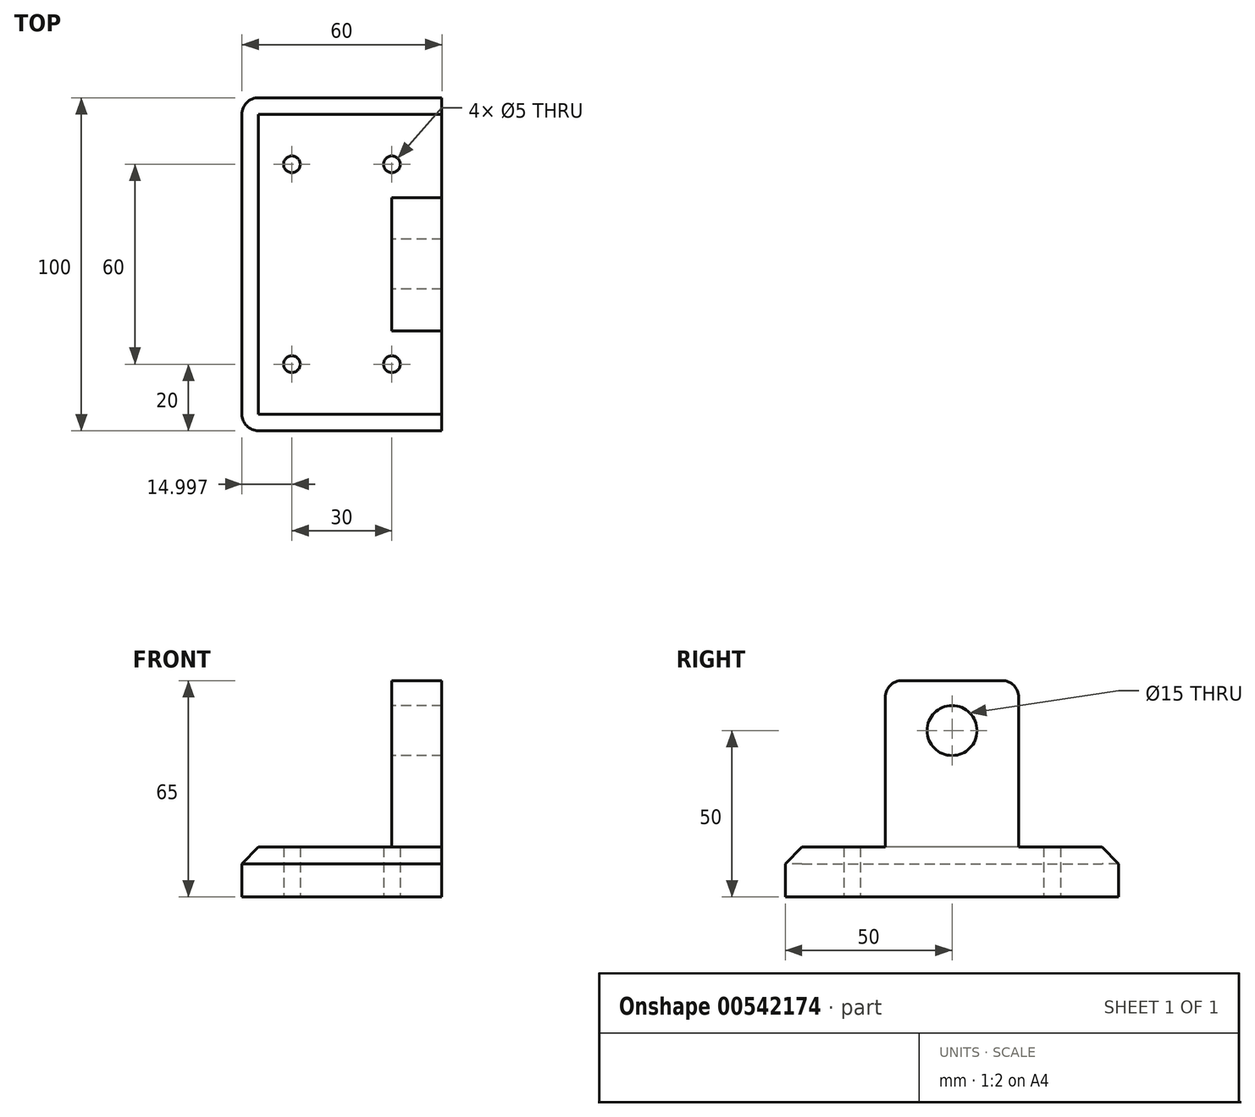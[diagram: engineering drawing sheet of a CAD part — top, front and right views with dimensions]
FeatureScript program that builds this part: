
annotation { "Feature Type Name" : "Feature", "Feature Type Description" : "" }
export const myFeature = defineFeature(function(context is Context, id is Id, definition is map)
    precondition{}
    {
        {
            var Q0;
            Q0=qCreatedBy(makeId("Top.planeOp"),FACE);
            var sketch = newSketch(context, id + "F0", { "sketchPlane" : qUnion([Q0])});
            skLineSegment(sketch, "E0.bottom", {"start": v(-60.08, 51.59) * mm, "end": v(-5.08, 51.59) * mm});
            skLineSegment(sketch, "E0.top", {"start": v(-60.08, -48.41) * mm, "end": v(-5.08, -48.41) * mm});
            skLineSegment(sketch, "E0.left", {"start": v(-65.08, 46.59) * mm, "end": v(-65.08, -43.41) * mm});
            skLineSegment(sketch, "E0.right", {"start": v(-5.08, 51.59) * mm, "end": v(-5.08, -48.41) * mm});
            skPoint(sketch, "E1.visualSharp", {"position": v(-65.08, 51.59) * mm});
            skArc(sketch, "E1.filletArc", {"start": v(-60.08, 51.59) * mm, "mid": v(-63.62, 50.13) * mm, "end": v(-65.08, 46.59) * mm});
            skPoint(sketch, "E2.visualSharp", {"position": v(-65.08, -48.41) * mm});
            skArc(sketch, "E2.filletArc", {"start": v(-65.08, -43.41) * mm, "mid": v(-63.62, -46.95) * mm, "end": v(-60.08, -48.41) * mm});
            skSolve(sketch);
        }
        {
            var Q0;
            Q0 = qSketchRegion(id + "F0", true);
            extrude(context, id + "F1", {"entities" : qUnion([Q0]), "depth" : 15 * mm, "offsetDistance" : 25 * mm});
        }
        {
            var Q0;
            Q0=makeQuery(id+"F1.opExtrude","SWEPT_FACE",FACE,{"disambiguationData":[OSD([sQuery(id+"F0.wireOp",EDGE,"E0.right")])]});
            var sketch = newSketch(context, id + "F2", { "sketchPlane" : qUnion([Q0])});
            skLineSegment(sketch, "E3.bottom", {"start": v(-18.41, 15) * mm, "end": v(21.59, 15) * mm});
            skLineSegment(sketch, "E3.top", {"start": v(-18.41, 65) * mm, "end": v(21.59, 65) * mm});
            skLineSegment(sketch, "E3.left", {"start": v(-18.41, 15) * mm, "end": v(-18.41, 65) * mm});
            skLineSegment(sketch, "E3.right", {"start": v(21.59, 15) * mm, "end": v(21.59, 65) * mm});
            skSolve(sketch);
        }
        {
            var Q0;
            Q0=makeQuery(id+"F2.imprint","IMPRINT",FACE,{"disambiguationData":[TD([[makeQuery(id+"F2.imprint","IMPRINT",EDGE,{"derivedFrom":sQuery(id+"F2.wireOp",EDGE,"E3.bottom")}),-1.0]])]});
            extrude(context, id + "F3", {"entities" : qUnion([Q0]), "operationType" : NewBodyOperationType.ADD, "oppositeDirection" : true, "depth" : 15 * mm, "offsetDistance" : 25 * mm});
        }
        {
            var Q0;
            Q0=makeQuery(id+"F3.opExtrude","SWEPT_EDGE",EDGE,{"disambiguationData":[OSD([sQuery(id+"F2.wireOp",EDGE,"E3.top"),sQuery(id+"F2.wireOp",EDGE,"E3.right")])]});
            var Q1;
            Q1=makeQuery(id+"F3.opExtrude","SWEPT_EDGE",EDGE,{"disambiguationData":[OSD([sQuery(id+"F2.wireOp",EDGE,"E3.top"),sQuery(id+"F2.wireOp",EDGE,"E3.left")])]});
            var Q2;
            Q2=makeQuery(id+"F3.opExtrude","SWEPT_EDGE",EDGE,{"disambiguationData":[OSD([sQuery(id+"F0.wireOp",EDGE,"E0.right"),sQuery(id+"F2.wireOp",EDGE,"E3.bottom"),sQuery(id+"F2.wireOp",EDGE,"E3.left")])]});
            var Q3;
            Q3=makeQuery(id+"F3.opExtrude","CAP_EDGE",EDGE,{"disambiguationData":[OSD([sQuery(id+"F2.wireOp",EDGE,"E3.bottom")])],"isStart":false});
            var Q4;
            Q4=makeQuery(id+"F3.opExtrude","SWEPT_EDGE",EDGE,{"disambiguationData":[OSD([sQuery(id+"F0.wireOp",EDGE,"E0.right"),sQuery(id+"F2.wireOp",EDGE,"E3.bottom"),sQuery(id+"F2.wireOp",EDGE,"E3.right")])]});
            fillet(context, id + "F4", {"entities" : qUnion([Q0, Q1, Q2, Q3, Q4]), "radius" : 5 * mm, "tangentPropagation" : true, "allowEdgeOverflow" : false});
        }
        {
            var Q0;
            Q0=makeQuery(id+"F1.opExtrude","CAP_EDGE",EDGE,{"disambiguationData":[OSD([sQuery(id+"F0.wireOp",EDGE,"E0.bottom")])],"isStart":false});
            chamfer(context, id + "F5", {"entities" : qUnion([Q0]), "width" : 5 * mm, "tangentPropagation" : true});
        }
        {
            var Q0;
            Q0=makeQuery(id+"F3.opExtrude","CAP_FACE",FACE,{"disambiguationData":[OSD([sQuery(id+"F2.wireOp",EDGE,"E3.bottom"),sQuery(id+"F2.wireOp",EDGE,"E3.top"),sQuery(id+"F2.wireOp",EDGE,"E3.left"),sQuery(id+"F2.wireOp",EDGE,"E3.right")])],"isStart":false});
            var sketch = newSketch(context, id + "F6", { "sketchPlane" : qUnion([Q0])});
            skLineSegment(sketch, "E4", {"start": v(-1.59, 65) * mm, "end": v(-1.59, 20) * mm, "construction": true});
            skCircle(sketch, "E5", {"center": v(-1.59, 50) * mm, "radius": 7.5 * mm});
            skSolve(sketch);
        }
        {
            var Q0;
            Q0=makeQuery(id+"F6.imprint","IMPRINT",FACE,{"disambiguationData":[TD([[makeQuery(id+"F6.imprint","IMPRINT",EDGE,{"derivedFrom":sQuery(id+"F6.wireOp",EDGE,"E5")}),1.0]])]});
            extrude(context, id + "F7", {"entities" : qUnion([Q0]), "operationType" : NewBodyOperationType.REMOVE, "oppositeDirection" : true, "depth" : 25 * mm, "offsetDistance" : 25 * mm});
        }
        {
            var Q0;
            Q0=makeQuery(id+"F1.opExtrude","CAP_FACE",FACE,{"disambiguationData":[OSD([sQuery(id+"F0.wireOp",EDGE,"E0.bottom"),sQuery(id+"F0.wireOp",EDGE,"E0.top"),sQuery(id+"F0.wireOp",EDGE,"E0.left"),sQuery(id+"F0.wireOp",EDGE,"E0.right"),sQuery(id+"F0.wireOp",EDGE,"E1.filletArc"),sQuery(id+"F0.wireOp",EDGE,"E2.filletArc")])],"isStart":true});
            var sketch = newSketch(context, id + "F8", { "sketchPlane" : qUnion([Q0])});
            skCircle(sketch, "E6", {"center": v(-50.08, 28.41) * mm, "radius": 2.5 * mm});
            skCircle(sketch, "E7.0.1.0", {"center": v(-50.08, -31.59) * mm, "radius": 2.5 * mm});
            skCircle(sketch, "E7.1.0.0", {"center": v(-20.08, 28.41) * mm, "radius": 2.5 * mm});
            skCircle(sketch, "E7.1.1.0", {"center": v(-20.08, -31.59) * mm, "radius": 2.5 * mm});
            skLineSegment(sketch, "E7.direction1", {"start": v(-50.08, 28.41) * mm, "end": v(-20.08, 28.41) * mm, "construction": true});
            skLineSegment(sketch, "E7.direction2", {"start": v(-50.08, 28.41) * mm, "end": v(-50.08, -31.59) * mm, "construction": true});
            skSolve(sketch);
        }
        {
            var Q0;
            Q0=makeQuery(id+"F8.imprint","IMPRINT",FACE,{"disambiguationData":[TD([[makeQuery(id+"F8.imprint","IMPRINT",EDGE,{"derivedFrom":sQuery(id+"F8.wireOp",EDGE,"E7.1.1.0")}),1.0]])]});
            var Q1;
            Q1=makeQuery(id+"F8.imprint","IMPRINT",FACE,{"disambiguationData":[TD([[makeQuery(id+"F8.imprint","IMPRINT",EDGE,{"derivedFrom":sQuery(id+"F8.wireOp",EDGE,"E7.0.1.0")}),1.0]])]});
            var Q2;
            Q2=makeQuery(id+"F8.imprint","IMPRINT",FACE,{"disambiguationData":[TD([[makeQuery(id+"F8.imprint","IMPRINT",EDGE,{"derivedFrom":sQuery(id+"F8.wireOp",EDGE,"E6")}),1.0]])]});
            var Q3;
            Q3=makeQuery(id+"F8.imprint","IMPRINT",FACE,{"disambiguationData":[TD([[makeQuery(id+"F8.imprint","IMPRINT",EDGE,{"derivedFrom":sQuery(id+"F8.wireOp",EDGE,"E7.1.0.0")}),1.0]])]});
            extrude(context, id + "F9", {"entities" : qUnion([Q0, Q1, Q2, Q3]), "operationType" : NewBodyOperationType.REMOVE, "oppositeDirection" : true, "depth" : 25 * mm, "offsetDistance" : 25 * mm});
        }
    });
